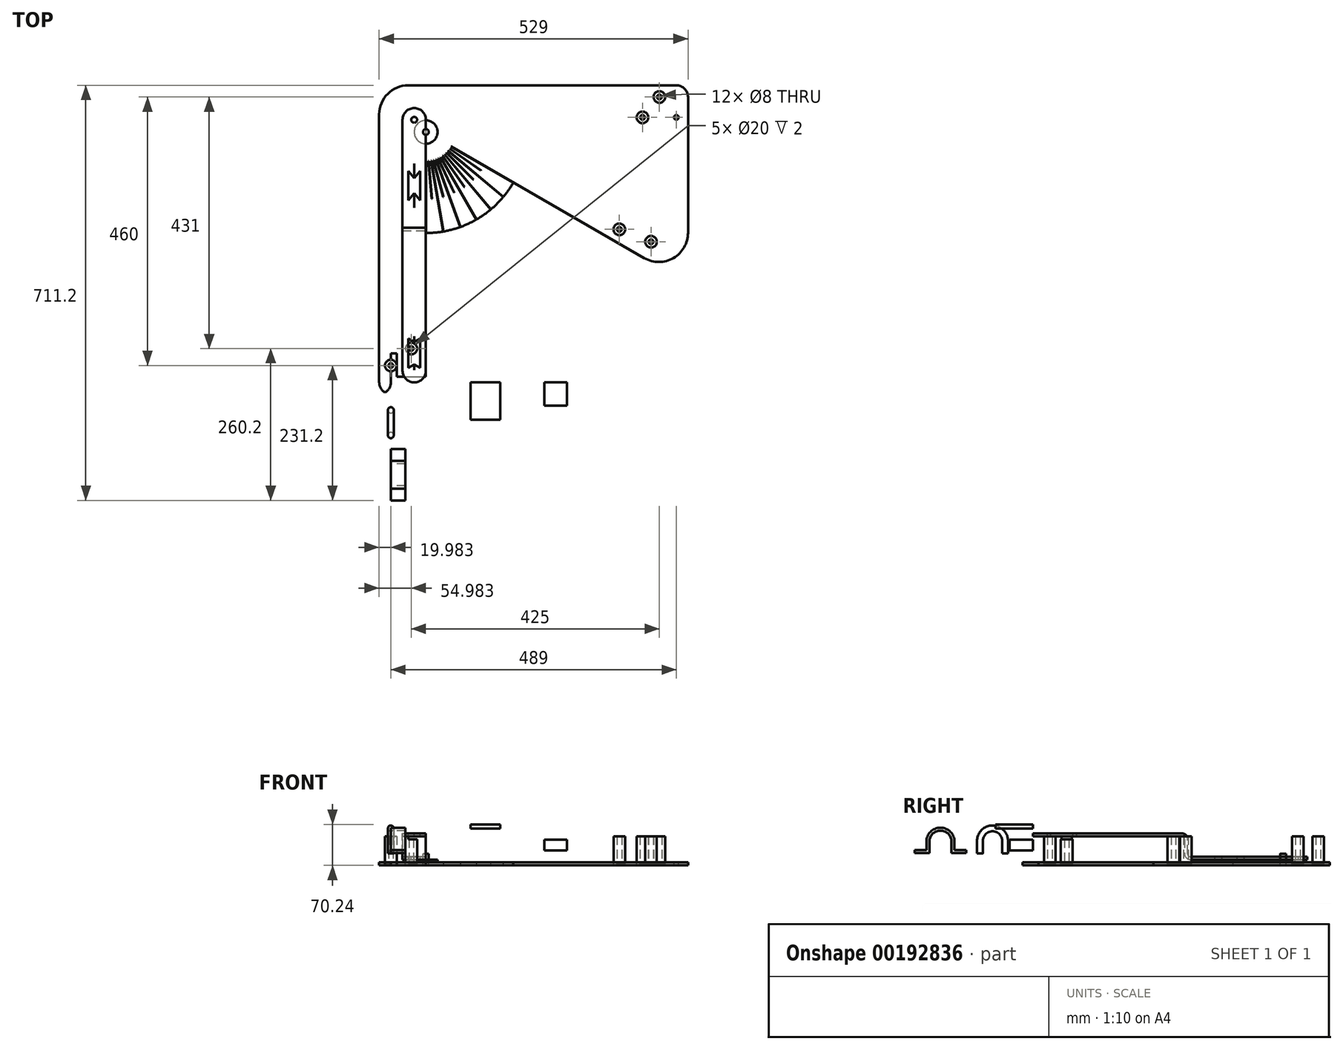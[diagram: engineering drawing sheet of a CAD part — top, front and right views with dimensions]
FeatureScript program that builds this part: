
annotation { "Feature Type Name" : "Feature", "Feature Type Description" : "" }
export const myFeature = defineFeature(function(context is Context, id is Id, definition is map)
    precondition{}
    {
        {
            var Q0;
            Q0=qCreatedBy(makeId("Top.planeOp"),FACE);
            var sketch = newSketch(context, id + "F0", { "sketchPlane" : qUnion([Q0])});
            skLineSegment(sketch, "E0.bottom", {"start": v(0, 0) * mm, "end": v(489, 0) * mm});
            skLineSegment(sketch, "E0.left", {"start": v(0, 0) * mm, "end": v(0, 500) * mm});
            skLineSegment(sketch, "E0.right", {"start": v(489, 0) * mm, "end": v(489, 479) * mm});
            skLineSegment(sketch, "E1.top", {"start": v(0, 0) * mm, "end": v(10, 0) * mm});
            skLineSegment(sketch, "E1.left", {"start": v(0, 489) * mm, "end": v(0, 0) * mm});
            skLineSegment(sketch, "E1.right", {"start": v(10, 50) * mm, "end": v(10, 10) * mm});
            skPoint(sketch, "E2", {"position": v(60, 429) * mm});
            skLineSegment(sketch, "E3", {"start": v(60, 255.9) * mm, "end": v(60, 0) * mm});
            skLineSegment(sketch, "E4", {"start": v(209.9, 342.45) * mm, "end": v(489, 181.32) * mm});
            skLineSegment(sketch, "E5.bottom", {"start": v(10, 48) * mm, "end": v(60, 48) * mm, "construction": true});
            skLineSegment(sketch, "E5.right", {"start": v(60, 48) * mm, "end": v(60, 10) * mm, "construction": true});
            skLineSegment(sketch, "E6.top", {"start": v(441, 429) * mm, "end": v(479, 429) * mm, "construction": true});
            skLineSegment(sketch, "E6.left", {"start": v(441, 479) * mm, "end": v(441, 429) * mm, "construction": true});
            skArc(sketch, "E7", {"start": v(60, 29) * mm, "mid": v(342.84, 146.16) * mm, "end": v(460, 429) * mm, "construction": true});
            skPoint(sketch, "E8", {"position": v(10, 29) * mm});
            skPoint(sketch, "E9", {"position": v(460, 479) * mm});
            skArc(sketch, "E10.0", {"start": v(60, 10) * mm, "mid": v(356.28, 132.72) * mm, "end": v(479, 429) * mm, "construction": true});
            skArc(sketch, "E11.0", {"start": v(60, 48) * mm, "mid": v(329.4, 159.6) * mm, "end": v(441, 429) * mm, "construction": true});
            skLineSegment(sketch, "E12", {"start": v(60, 255.9) * mm, "end": v(209.9, 342.45) * mm, "construction": true});
            skPoint(sketch, "E13.end.orphan", {"position": v(189.9, 354) * mm});
            skPoint(sketch, "E13.start.orphan", {"position": v(60, 279) * mm});
            skCircle(sketch, "E14", {"center": v(60, 429) * mm, "radius": 5 * mm});
            skLineSegment(sketch, "E15.top", {"start": v(489, 489) * mm, "end": v(0, 489) * mm});
            skLineSegment(sketch, "E15.left", {"start": v(489, 479) * mm, "end": v(489, 489) * mm});
            skLineSegment(sketch, "E16", {"start": v(439, 489) * mm, "end": v(439, 479) * mm});
            skLineSegment(sketch, "E17", {"start": v(439, 479) * mm, "end": v(479, 479) * mm});
            skLineSegment(sketch, "E18", {"start": v(479, 479) * mm, "end": v(479, 429) * mm});
            skLineSegment(sketch, "E19", {"start": v(489, 429) * mm, "end": v(479, 429) * mm});
            skArc(sketch, "E20", {"start": v(60, 255.9) * mm, "mid": v(146.55, 279.1) * mm, "end": v(209.9, 342.45) * mm});
            skLineSegment(sketch, "E21", {"start": v(0, 50) * mm, "end": v(10, 50) * mm});
            skLineSegment(sketch, "E22", {"start": v(10, 10) * mm, "end": v(60, 10) * mm});
            skLineSegment(sketch, "E23", {"start": v(60, 0) * mm, "end": v(60, -20) * mm});
            skLineSegment(sketch, "E24", {"start": v(60, -20) * mm, "end": v(0, -20) * mm});
            skLineSegment(sketch, "E25", {"start": v(0, -20) * mm, "end": v(0, 0) * mm});
            skLineSegment(sketch, "E26", {"start": v(0, 489) * mm, "end": v(-20, 489) * mm});
            skLineSegment(sketch, "E27", {"start": v(-20, 489) * mm, "end": v(-20, -20) * mm});
            skLineSegment(sketch, "E28", {"start": v(-20, -20) * mm, "end": v(0, -20) * mm});
            skLineSegment(sketch, "E29", {"start": v(489, 181.32) * mm, "end": v(509, 169.77) * mm});
            skLineSegment(sketch, "E30", {"start": v(509, 169.77) * mm, "end": v(509, 489) * mm});
            skLineSegment(sketch, "E31", {"start": v(509, 489) * mm, "end": v(489, 489) * mm});
            skLineSegment(sketch, "E32", {"start": v(509, 489) * mm, "end": v(509, 509) * mm});
            skLineSegment(sketch, "E33", {"start": v(509, 509) * mm, "end": v(-20, 509) * mm});
            skLineSegment(sketch, "E34", {"start": v(-20, 509) * mm, "end": v(-20, 489) * mm});
            skSolve(sketch);
        }
        {
            var Q0;
            {var subQ3=sQuery(id+"F0.wireOp",EDGE,"E1.right");Q0=makeQuery(id+"F0.imprint","IMPRINT",FACE,{"disambiguationData":[TD([[makeQuery(id+"F0.imprint","IMPRINT",EDGE,{"derivedFrom":subQ3}),1.0]])]});}
            var Q1;
            {var subQ2=sQuery(id+"F0.wireOp",EDGE,"E1.top");Q1=makeQuery(id+"F0.imprint","IMPRINT",FACE,{"disambiguationData":[TD([[makeQuery(id+"F0.imprint","IMPRINT",EDGE,{"derivedFrom":subQ2}),1.0]])]});}
            var Q2;
            {var subQ1=sQuery(id+"F0.wireOp",EDGE,"E15.left");Q2=makeQuery(id+"F0.imprint","IMPRINT",FACE,{"disambiguationData":[TD([[makeQuery(id+"F0.imprint","IMPRINT",EDGE,{"derivedFrom":subQ1}),1.0]])]});}
            var Q3;
            {var subQ1=sQuery(id+"F0.wireOp",EDGE,"E25");Q3=makeQuery(id+"F0.imprint","IMPRINT",FACE,{"disambiguationData":[TD([[makeQuery(id+"F0.imprint","IMPRINT",EDGE,{"derivedFrom":subQ1}),1.0]])]});}
            var Q4;
            {var subQ0=sQuery(id+"F0.wireOp",EDGE,"E1.top");Q4=makeQuery(id+"F0.imprint","IMPRINT",FACE,{"disambiguationData":[TD([[makeQuery(id+"F0.imprint","IMPRINT",EDGE,{"derivedFrom":subQ0}),-1.0]])]});}
            var Q5;
            {var subQ3=sQuery(id+"F0.wireOp",EDGE,"E26");Q5=makeQuery(id+"F0.imprint","IMPRINT",FACE,{"disambiguationData":[TD([[makeQuery(id+"F0.imprint","IMPRINT",EDGE,{"derivedFrom":subQ3}),-1.0]])]});}
            var Q6;
            {var subQ1=sQuery(id+"F0.wireOp",EDGE,"E15.left");Q6=makeQuery(id+"F0.imprint","IMPRINT",FACE,{"disambiguationData":[TD([[makeQuery(id+"F0.imprint","IMPRINT",EDGE,{"derivedFrom":subQ1}),-1.0]])]});}
            extrude(context, id + "F1", {"entities" : qUnion([Q0, Q1, Q2, Q3, Q4, Q5, Q6]), "depth" : 5 * mm});
        }
        {
            var Q0;
            Q0=makeQuery(id+"F1.opExtrude","SWEPT_FACE",FACE,{"disambiguationData":[OSD([sQuery(id+"F0.wireOp",EDGE,"E33")])]});
            cPlane(context, id + "F2", {"entities" : qUnion([Q0]), "cplaneType" : CPlaneType.OFFSET, "offset" : 80 * mm, "oppositeDirection" : true, "width" : 150 * mm, "height" : 150 * mm});
        }
        {
            var Q0;
            Q0=qCreatedBy(id+"F2.planeOp",FACE);
            var sketch = newSketch(context, id + "F3", { "sketchPlane" : qUnion([Q0])});
            skLineSegment(sketch, "E35", {"start": v(-60, 20) * mm, "end": v(-60, 0) * mm});
            skLineSegment(sketch, "E36", {"start": v(-60, 20) * mm, "end": v(-65, 20) * mm});
            skLineSegment(sketch, "E37", {"start": v(-65, 20) * mm, "end": v(-65, 10) * mm});
            skLineSegment(sketch, "E38", {"start": v(-65, 10) * mm, "end": v(-80, 10) * mm});
            skLineSegment(sketch, "E39", {"start": v(-80, 10) * mm, "end": v(-80, 5) * mm});
            skLineSegment(sketch, "E40", {"start": v(-80, 5) * mm, "end": v(-65, 5) * mm});
            skLineSegment(sketch, "E41", {"start": v(-65, 5) * mm, "end": v(-65, 0) * mm});
            skLineSegment(sketch, "E42", {"start": v(-65, 0) * mm, "end": v(-60, 0) * mm});
            skSolve(sketch);
        }
        {
            var Q0;
            Q0=qSketchRegion(id+"F3",true);
            var Q1;
            Q1=sQuery(id+"F3.wireOp",EDGE,"E35");
            revolve(context, id + "F4", {"entities" : qUnion([Q0]), "axis" : qUnion([Q1]), "revolveType" : RevolveType.FULL});
        }
        {
            var Q0;
            Q0=makeQuery(id+"F1.opExtrude","CAP_FACE",FACE,{"disambiguationData":[OSD([sQuery(id+"F0.wireOp",EDGE,"E0.bottom"),sQuery(id+"F0.wireOp",EDGE,"E0.top"),sQuery(id+"F0.wireOp",EDGE,"E0.right"),sQuery(id+"F0.wireOp",EDGE,"E1.right"),sQuery(id+"F0.wireOp",EDGE,"E3"),sQuery(id+"F0.wireOp",EDGE,"E4"),sQuery(id+"F0.wireOp",EDGE,"E12"),sQuery(id+"F0.wireOp",EDGE,"E14")])],"isStart":false});
            cPlane(context, id + "F5", {"entities" : qUnion([Q0]), "cplaneType" : CPlaneType.OFFSET, "offset" : 0 * mm, "width" : 150 * mm, "height" : 150 * mm});
        }
        {
            var Q0;
            Q0=qCreatedBy(id+"F5.planeOp",FACE);
            var sketch = newSketch(context, id + "F6", { "sketchPlane" : qUnion([Q0])});
            skCircle(sketch, "E43", {"center": v(34.98, 58) * mm, "radius": 10 * mm});
            skLineSegment(sketch, "E44.bottom", {"start": v(9.98, 10) * mm, "end": v(59.98, 10) * mm, "construction": true});
            skLineSegment(sketch, "E44.top", {"start": v(9.98, 48) * mm, "end": v(59.98, 48) * mm, "construction": true});
            skLineSegment(sketch, "E44.left", {"start": v(9.98, 10) * mm, "end": v(9.98, 48) * mm, "construction": true});
            skLineSegment(sketch, "E44.right", {"start": v(59.98, 10) * mm, "end": v(59.98, 48) * mm, "construction": true});
            skLineSegment(sketch, "E45.bottom", {"start": v(478.98, 479) * mm, "end": v(440.98, 479) * mm, "construction": true});
            skLineSegment(sketch, "E45.top", {"start": v(478.98, 429) * mm, "end": v(440.98, 429) * mm, "construction": true});
            skLineSegment(sketch, "E45.left", {"start": v(478.98, 479) * mm, "end": v(478.98, 429) * mm, "construction": true});
            skLineSegment(sketch, "E45.right", {"start": v(440.98, 479) * mm, "end": v(440.98, 429) * mm, "construction": true});
            skArc(sketch, "E46", {"start": v(59.98, 29) * mm, "mid": v(342.83, 146.16) * mm, "end": v(459.98, 429) * mm, "construction": true});
            skArc(sketch, "E47.0", {"start": v(59.98, 10) * mm, "mid": v(356.26, 132.72) * mm, "end": v(478.98, 429) * mm, "construction": true});
            skArc(sketch, "E48.0", {"start": v(59.98, 48) * mm, "mid": v(329.4, 159.6) * mm, "end": v(440.98, 429) * mm, "construction": true});
            skLineSegment(sketch, "E49", {"start": v(459.98, 429) * mm, "end": v(459.98, 479) * mm, "construction": true});
            skLineSegment(sketch, "E50", {"start": v(59.98, 29) * mm, "end": v(9.98, 29) * mm, "construction": true});
            skCircle(sketch, "E51", {"center": v(430.98, 454) * mm, "radius": 10 * mm});
            skCircle(sketch, "E52", {"center": v(445.6, 241.01) * mm, "radius": 10 * mm});
            skLineSegment(sketch, "E53", {"start": v(445.6, 241.01) * mm, "end": v(391.37, 262.2) * mm, "construction": true});
            skCircle(sketch, "E54", {"center": v(391.37, 262.2) * mm, "radius": 10 * mm});
            skCircle(sketch, "E55.MirrorC", {"center": v(34.98, 0) * mm, "radius": 10 * mm});
            skCircle(sketch, "E56", {"center": v(-0.02, 29) * mm, "radius": 10 * mm});
            skLineSegment(sketch, "E57", {"start": v(34.98, 0) * mm, "end": v(34.98, 48) * mm, "construction": true});
            skCircle(sketch, "E58.MirrorC", {"center": v(488.98, 454) * mm, "radius": 10 * mm});
            skLineSegment(sketch, "E59", {"start": v(430.98, 454) * mm, "end": v(488.98, 454) * mm, "construction": true});
            skCircle(sketch, "E60", {"center": v(459.98, 489) * mm, "radius": 10 * mm});
            skCircle(sketch, "E61", {"center": v(459.98, 489) * mm, "radius": 4 * mm});
            skCircle(sketch, "E62", {"center": v(488.98, 454) * mm, "radius": 4 * mm});
            skCircle(sketch, "E63", {"center": v(430.98, 454) * mm, "radius": 4 * mm});
            skCircle(sketch, "E64", {"center": v(445.6, 241.01) * mm, "radius": 4 * mm});
            skCircle(sketch, "E65", {"center": v(391.37, 262.2) * mm, "radius": 4 * mm});
            skCircle(sketch, "E66", {"center": v(34.98, 58) * mm, "radius": 4 * mm});
            skCircle(sketch, "E67", {"center": v(34.98, 0) * mm, "radius": 4 * mm});
            skCircle(sketch, "E68", {"center": v(-0.02, 29) * mm, "radius": 4 * mm});
            skSolve(sketch);
        }
        {
            var Q0;
            Q0=makeQuery(id+"F6.imprint","IMPRINT",FACE,{"disambiguationData":[TD([[makeQuery(id+"F6.imprint","IMPRINT",EDGE,{"derivedFrom":sQuery(id+"F6.wireOp",EDGE,"E58.MirrorC")}),-1.0]])]});
            var Q1;
            Q1=makeQuery(id+"F6.imprint","IMPRINT",FACE,{"disambiguationData":[TD([[makeQuery(id+"F6.imprint","IMPRINT",EDGE,{"derivedFrom":sQuery(id+"F6.wireOp",EDGE,"E60")}),1.0]])]});
            var Q2;
            Q2=makeQuery(id+"F6.imprint","IMPRINT",FACE,{"disambiguationData":[TD([[makeQuery(id+"F6.imprint","IMPRINT",EDGE,{"derivedFrom":sQuery(id+"F6.wireOp",EDGE,"E51")}),1.0]])]});
            var Q3;
            Q3=makeQuery(id+"F6.imprint","IMPRINT",FACE,{"disambiguationData":[TD([[makeQuery(id+"F6.imprint","IMPRINT",EDGE,{"derivedFrom":sQuery(id+"F6.wireOp",EDGE,"E52")}),1.0]])]});
            var Q4;
            Q4=makeQuery(id+"F6.imprint","IMPRINT",FACE,{"disambiguationData":[TD([[makeQuery(id+"F6.imprint","IMPRINT",EDGE,{"derivedFrom":sQuery(id+"F6.wireOp",EDGE,"E54")}),1.0]])]});
            var Q5;
            Q5=makeQuery(id+"F6.imprint","IMPRINT",FACE,{"disambiguationData":[TD([[makeQuery(id+"F6.imprint","IMPRINT",EDGE,{"derivedFrom":sQuery(id+"F6.wireOp",EDGE,"E55.MirrorC")}),-1.0]])]});
            var Q6;
            Q6=makeQuery(id+"F6.imprint","IMPRINT",FACE,{"disambiguationData":[TD([[makeQuery(id+"F6.imprint","IMPRINT",EDGE,{"derivedFrom":sQuery(id+"F6.wireOp",EDGE,"E43")}),1.0]])]});
            var Q7;
            Q7=makeQuery(id+"F6.imprint","IMPRINT",FACE,{"disambiguationData":[TD([[makeQuery(id+"F6.imprint","IMPRINT",EDGE,{"derivedFrom":sQuery(id+"F6.wireOp",EDGE,"E56")}),1.0]])]});
            extrude(context, id + "F7", {"entities" : qUnion([Q0, Q1, Q2, Q3, Q4, Q5, Q6, Q7]), "operationType" : NewBodyOperationType.REMOVE, "oppositeDirection" : true, "depth" : 2 * mm});
        }
        {
            var Q0;
            Q0=makeQuery(id+"F6.imprint","IMPRINT",FACE,{"disambiguationData":[TD([[makeQuery(id+"F6.imprint","IMPRINT",EDGE,{"derivedFrom":sQuery(id+"F6.wireOp",EDGE,"E58.MirrorC")}),-1.0]])]});
            var Q1;
            Q1=makeQuery(id+"F6.imprint","IMPRINT",FACE,{"disambiguationData":[TD([[makeQuery(id+"F6.imprint","IMPRINT",EDGE,{"derivedFrom":sQuery(id+"F6.wireOp",EDGE,"E60")}),1.0]])]});
            var Q2;
            Q2=makeQuery(id+"F6.imprint","IMPRINT",FACE,{"disambiguationData":[TD([[makeQuery(id+"F6.imprint","IMPRINT",EDGE,{"derivedFrom":sQuery(id+"F6.wireOp",EDGE,"E51")}),1.0]])]});
            var Q3;
            Q3=makeQuery(id+"F6.imprint","IMPRINT",FACE,{"disambiguationData":[TD([[makeQuery(id+"F6.imprint","IMPRINT",EDGE,{"derivedFrom":sQuery(id+"F6.wireOp",EDGE,"E52")}),1.0]])]});
            var Q4;
            Q4=makeQuery(id+"F6.imprint","IMPRINT",FACE,{"disambiguationData":[TD([[makeQuery(id+"F6.imprint","IMPRINT",EDGE,{"derivedFrom":sQuery(id+"F6.wireOp",EDGE,"E54")}),1.0]])]});
            var Q5;
            Q5=makeQuery(id+"F6.imprint","IMPRINT",FACE,{"disambiguationData":[TD([[makeQuery(id+"F6.imprint","IMPRINT",EDGE,{"derivedFrom":sQuery(id+"F6.wireOp",EDGE,"E56")}),1.0]])]});
            var Q6;
            Q6=makeQuery(id+"F6.imprint","IMPRINT",FACE,{"disambiguationData":[TD([[makeQuery(id+"F6.imprint","IMPRINT",EDGE,{"derivedFrom":sQuery(id+"F6.wireOp",EDGE,"E55.MirrorC")}),-1.0]])]});
            var Q7;
            Q7=makeQuery(id+"F6.imprint","IMPRINT",FACE,{"disambiguationData":[TD([[makeQuery(id+"F6.imprint","IMPRINT",EDGE,{"derivedFrom":sQuery(id+"F6.wireOp",EDGE,"E43")}),1.0]])]});
            extrude(context, id + "F8", {"entities" : qUnion([Q0, Q1, Q2, Q3, Q4, Q5, Q6, Q7]), "depth" : 44.85 * mm});
        }
        {
            var Q0;
            Q0=makeQuery(id+"F1.opExtrude","CAP_FACE",FACE,{"disambiguationData":[OSD([sQuery(id+"F0.wireOp",EDGE,"E0.bottom"),sQuery(id+"F0.wireOp",EDGE,"E0.right"),sQuery(id+"F0.wireOp",EDGE,"E1.right"),sQuery(id+"F0.wireOp",EDGE,"E3"),sQuery(id+"F0.wireOp",EDGE,"E4"),sQuery(id+"F0.wireOp",EDGE,"E12"),sQuery(id+"F0.wireOp",EDGE,"E14"),sQuery(id+"F0.wireOp",EDGE,"E15.top"),sQuery(id+"F0.wireOp",EDGE,"E16"),sQuery(id+"F0.wireOp",EDGE,"E17"),sQuery(id+"F0.wireOp",EDGE,"E18"),sQuery(id+"F0.wireOp",EDGE,"E19")])],"isStart":false});
            var sketch = newSketch(context, id + "F9", { "sketchPlane" : qUnion([Q0])});
            skLineSegment(sketch, "E69", {"start": v(60, 379) * mm, "end": v(60, 255.9) * mm});
            skLineSegment(sketch, "E70", {"start": v(103.3, 404) * mm, "end": v(209.9, 342.45) * mm});
            skArc(sketch, "E71", {"start": v(60, 314) * mm, "mid": v(117.5, 329.4) * mm, "end": v(159.6, 371.5) * mm});
            skLineSegment(sketch, "E72.0", {"start": v(64.45, 426.72) * mm, "end": v(210.03, 342.67) * mm});
            skArc(sketch, "E73", {"start": v(60, 424) * mm, "mid": v(62.6, 424.73) * mm, "end": v(64.45, 426.72) * mm});
            skLineSegment(sketch, "E74.trimOffspring", {"start": v(64.2, 426.29) * mm, "end": v(64.83, 425.92) * mm});
            skLineSegment(sketch, "E75", {"start": v(210.03, 342.67) * mm, "end": v(209.9, 342.45) * mm});
            skLineSegment(sketch, "E76", {"start": v(100.96, 400.32) * mm, "end": v(154.2, 363.04) * mm});
            skLineSegment(sketch, "E77", {"start": v(98.3, 396.86) * mm, "end": v(192.6, 317.74) * mm});
            skLineSegment(sketch, "E78", {"start": v(95.36, 393.64) * mm, "end": v(141.32, 347.68) * mm});
            skLineSegment(sketch, "E79", {"start": v(92.14, 390.7) * mm, "end": v(171.26, 296.4) * mm});
            skLineSegment(sketch, "E80", {"start": v(88.68, 388.04) * mm, "end": v(125.96, 334.8) * mm});
            skLineSegment(sketch, "E81", {"start": v(85, 385.7) * mm, "end": v(146.55, 279.1) * mm});
            skLineSegment(sketch, "E82", {"start": v(81.13, 383.68) * mm, "end": v(108.6, 324.77) * mm});
            skLineSegment(sketch, "E83", {"start": v(77.1, 382.02) * mm, "end": v(119.2, 266.34) * mm});
            skLineSegment(sketch, "E84", {"start": v(72.94, 380.7) * mm, "end": v(89.76, 317.92) * mm});
            skLineSegment(sketch, "E85", {"start": v(68.68, 379.76) * mm, "end": v(90.06, 258.54) * mm});
            skLineSegment(sketch, "E86", {"start": v(64.36, 379.2) * mm, "end": v(70.02, 314.44) * mm});
            skArc(sketch, "E87", {"start": v(60, 255.9) * mm, "mid": v(146.55, 279.1) * mm, "end": v(209.9, 342.45) * mm, "construction": true});
            skPoint(sketch, "E88.orphan", {"position": v(117.5, 329.4) * mm});
            skLineSegment(sketch, "E89.0", {"start": v(64.24, 426.34) * mm, "end": v(64.83, 425.92) * mm});
            skLineSegment(sketch, "E90.0", {"start": v(63.95, 425.93) * mm, "end": v(64.55, 425.51) * mm});
            skLineSegment(sketch, "E91.0", {"start": v(63.67, 425.6) * mm, "end": v(64.23, 425.13) * mm});
            skLineSegment(sketch, "E92.0", {"start": v(64, 425.98) * mm, "end": v(64.55, 425.51) * mm});
            skLineSegment(sketch, "E93.0", {"start": v(63.36, 425.29) * mm, "end": v(63.87, 424.77) * mm});
            skLineSegment(sketch, "E94.0", {"start": v(63.71, 425.64) * mm, "end": v(64.23, 425.13) * mm});
            skLineSegment(sketch, "E95.0", {"start": v(63.02, 425) * mm, "end": v(63.49, 424.45) * mm});
            skLineSegment(sketch, "E96.0", {"start": v(63.4, 425.33) * mm, "end": v(63.87, 424.77) * mm});
            skLineSegment(sketch, "E97.0", {"start": v(63.07, 425.05) * mm, "end": v(63.49, 424.45) * mm});
            skLineSegment(sketch, "E98.0", {"start": v(62.66, 424.76) * mm, "end": v(63.08, 424.17) * mm});
            skLineSegment(sketch, "E99.0", {"start": v(55.7, 435.96) * mm, "end": v(62.65, 423.92) * mm});
            skLineSegment(sketch, "E100.0", {"start": v(56.12, 436.21) * mm, "end": v(63.08, 424.17) * mm});
            skLineSegment(sketch, "E101.0", {"start": v(61.89, 424.36) * mm, "end": v(62.2, 423.7) * mm});
            skLineSegment(sketch, "E102.0", {"start": v(62.34, 424.57) * mm, "end": v(62.65, 423.92) * mm});
            skLineSegment(sketch, "E103.0", {"start": v(61.48, 424.22) * mm, "end": v(61.72, 423.53) * mm});
            skLineSegment(sketch, "E104.0", {"start": v(61.95, 424.39) * mm, "end": v(62.2, 423.7) * mm});
            skLineSegment(sketch, "E105.0", {"start": v(61.05, 424.1) * mm, "end": v(61.24, 423.4) * mm});
            skLineSegment(sketch, "E106.0", {"start": v(61.54, 424.24) * mm, "end": v(61.72, 423.53) * mm});
            skLineSegment(sketch, "E107.0", {"start": v(60.62, 424.03) * mm, "end": v(60.75, 423.32) * mm});
            skLineSegment(sketch, "E108.0", {"start": v(61.11, 424.12) * mm, "end": v(61.24, 423.4) * mm});
            skLineSegment(sketch, "E109.0", {"start": v(60.19, 424) * mm, "end": v(60.25, 423.27) * mm});
            skLineSegment(sketch, "E110.0", {"start": v(60.68, 424.04) * mm, "end": v(60.75, 423.32) * mm});
            skLineSegment(sketch, "E111.0", {"start": v(59.75, 429) * mm, "end": v(59.75, 255.9) * mm});
            skLineSegment(sketch, "E112.0", {"start": v(60.25, 424) * mm, "end": v(60.25, 423.27) * mm});
            skArc(sketch, "E113", {"start": v(103.3, 404) * mm, "mid": v(85, 385.7) * mm, "end": v(60, 379) * mm});
            skLineSegment(sketch, "E114.trimOffspring", {"start": v(60.25, 379) * mm, "end": v(60.25, 255.9) * mm});
            skLineSegment(sketch, "E115.trimOffspring", {"start": v(64.1, 379.17) * mm, "end": v(69.77, 314.42) * mm});
            skLineSegment(sketch, "E116.trimOffspring", {"start": v(64.6, 379.21) * mm, "end": v(70.27, 314.46) * mm});
            skLineSegment(sketch, "E117.trimOffspring", {"start": v(68.44, 379.72) * mm, "end": v(89.81, 258.5) * mm});
            skLineSegment(sketch, "E118.trimOffspring", {"start": v(68.93, 379.8) * mm, "end": v(90.3, 258.58) * mm});
            skLineSegment(sketch, "E119.trimOffspring", {"start": v(72.7, 380.64) * mm, "end": v(89.52, 317.85) * mm});
            skLineSegment(sketch, "E120.trimOffspring", {"start": v(73.18, 380.77) * mm, "end": v(90, 317.98) * mm});
            skLineSegment(sketch, "E121.trimOffspring", {"start": v(76.87, 381.93) * mm, "end": v(118.97, 266.26) * mm});
            skLineSegment(sketch, "E122.trimOffspring", {"start": v(77.34, 382.1) * mm, "end": v(119.44, 266.43) * mm});
            skLineSegment(sketch, "E123.trimOffspring", {"start": v(80.9, 383.58) * mm, "end": v(108.37, 324.67) * mm});
            skLineSegment(sketch, "E124.trimOffspring", {"start": v(81.36, 383.8) * mm, "end": v(108.83, 324.88) * mm});
            skLineSegment(sketch, "E125.trimOffspring", {"start": v(88.47, 387.9) * mm, "end": v(125.76, 334.65) * mm});
            skLineSegment(sketch, "E126.trimOffspring", {"start": v(88.88, 388.19) * mm, "end": v(126.17, 334.94) * mm});
            skLineSegment(sketch, "E127.trimOffspring", {"start": v(84.78, 385.57) * mm, "end": v(146.33, 278.97) * mm});
            skLineSegment(sketch, "E128.trimOffspring", {"start": v(85.22, 385.82) * mm, "end": v(146.76, 279.22) * mm});
            skLineSegment(sketch, "E129.trimOffspring", {"start": v(91.95, 390.54) * mm, "end": v(171.07, 296.24) * mm});
            skLineSegment(sketch, "E130.trimOffspring", {"start": v(92.33, 390.86) * mm, "end": v(171.45, 296.56) * mm});
            skLineSegment(sketch, "E131.trimOffspring", {"start": v(95.18, 393.47) * mm, "end": v(141.14, 347.5) * mm});
            skLineSegment(sketch, "E132.trimOffspring", {"start": v(95.53, 393.82) * mm, "end": v(141.5, 347.86) * mm});
            skLineSegment(sketch, "E133.trimOffspring", {"start": v(98.14, 396.67) * mm, "end": v(192.44, 317.55) * mm});
            skLineSegment(sketch, "E134.trimOffspring", {"start": v(98.46, 397.05) * mm, "end": v(192.76, 317.93) * mm});
            skLineSegment(sketch, "E135.trimOffspring", {"start": v(100.81, 400.12) * mm, "end": v(154.06, 362.83) * mm});
            skLineSegment(sketch, "E136.trimOffspring", {"start": v(101.1, 400.53) * mm, "end": v(154.35, 363.24) * mm});
            skLineSegment(sketch, "E137.trimOffspring", {"start": v(103.18, 403.78) * mm, "end": v(209.78, 342.24) * mm});
            skArc(sketch, "E138", {"start": v(209.9, 342.45) * mm, "mid": v(146.55, 279.1) * mm, "end": v(60, 255.9) * mm});
            skSolve(sketch);
        }
        {
            var Q0;
            {var subQ0=sQuery(id+"F9.wireOp",EDGE,"E113");var subQ1=sQuery(id+"F9.wireOp",EDGE,"E70");var subQ2=makeQuery(id+"F9.imprint","INTERSECT",VERTEX,{"derivedFrom":[subQ1,subQ0]});Q0=makeQuery(id+"F9.imprint","IMPRINT",FACE,{"disambiguationData":[TD([[makeQuery(id+"F9.imprint","IMPRINT",EDGE,{"disambiguationData":[TD([[subQ2,-1.0]])],"derivedFrom":subQ1}),-1.0]])]});}
            var Q1;
            {var subQ0=sQuery(id+"F9.wireOp",EDGE,"E70");var subQ3=sQuery(id+"F9.wireOp",EDGE,"E71");var subQ4=makeQuery(id+"F9.imprint","INTERSECT",VERTEX,{"derivedFrom":[subQ0,subQ3]});Q1=makeQuery(id+"F9.imprint","IMPRINT",FACE,{"disambiguationData":[TD([[makeQuery(id+"F9.imprint","IMPRINT",EDGE,{"disambiguationData":[TD([[subQ4,1.0]])],"derivedFrom":subQ3}),-1.0]])]});}
            var Q2;
            {var subQ0=sQuery(id+"F9.wireOp",EDGE,"E76");Q2=makeQuery(id+"F9.imprint","IMPRINT",FACE,{"disambiguationData":[TD([[makeQuery(id+"F9.imprint","IMPRINT",EDGE,{"derivedFrom":subQ0}),1.0]])]});}
            var Q3;
            {var subQ0=sQuery(id+"F9.wireOp",EDGE,"E76");Q3=makeQuery(id+"F9.imprint","IMPRINT",FACE,{"disambiguationData":[TD([[makeQuery(id+"F9.imprint","IMPRINT",EDGE,{"derivedFrom":subQ0}),-1.0]])]});}
            var Q4;
            {var subQ0=sQuery(id+"F9.wireOp",EDGE,"E77");var subQ1=sQuery(id+"F9.wireOp",EDGE,"E71");var subQ2=makeQuery(id+"F9.imprint","INTERSECT",VERTEX,{"derivedFrom":[subQ1,subQ0]});Q4=makeQuery(id+"F9.imprint","IMPRINT",FACE,{"disambiguationData":[TD([[makeQuery(id+"F9.imprint","IMPRINT",EDGE,{"disambiguationData":[TD([[subQ2,-1.0]])],"derivedFrom":subQ1}),1.0]])]});}
            var Q5;
            {var subQ0=sQuery(id+"F9.wireOp",EDGE,"E133.trimOffspring");var subQ1=sQuery(id+"F9.wireOp",EDGE,"E71");var subQ2=makeQuery(id+"F9.imprint","INTERSECT",VERTEX,{"derivedFrom":[subQ1,subQ0]});Q5=makeQuery(id+"F9.imprint","IMPRINT",FACE,{"disambiguationData":[TD([[makeQuery(id+"F9.imprint","IMPRINT",EDGE,{"disambiguationData":[TD([[subQ2,-1.0]])],"derivedFrom":subQ1}),1.0]])]});}
            var Q6;
            {var subQ0=sQuery(id+"F9.wireOp",EDGE,"E133.trimOffspring");var subQ1=sQuery(id+"F9.wireOp",EDGE,"E71");var subQ2=makeQuery(id+"F9.imprint","INTERSECT",VERTEX,{"derivedFrom":[subQ1,subQ0]});Q6=makeQuery(id+"F9.imprint","IMPRINT",FACE,{"disambiguationData":[TD([[makeQuery(id+"F9.imprint","IMPRINT",EDGE,{"disambiguationData":[TD([[subQ2,-1.0]])],"derivedFrom":subQ1}),-1.0]])]});}
            var Q7;
            {var subQ0=sQuery(id+"F9.wireOp",EDGE,"E77");var subQ1=sQuery(id+"F9.wireOp",EDGE,"E71");var subQ2=makeQuery(id+"F9.imprint","INTERSECT",VERTEX,{"derivedFrom":[subQ1,subQ0]});Q7=makeQuery(id+"F9.imprint","IMPRINT",FACE,{"disambiguationData":[TD([[makeQuery(id+"F9.imprint","IMPRINT",EDGE,{"disambiguationData":[TD([[subQ2,-1.0]])],"derivedFrom":subQ1}),-1.0]])]});}
            var Q8;
            {var subQ0=sQuery(id+"F9.wireOp",EDGE,"E78");Q8=makeQuery(id+"F9.imprint","IMPRINT",FACE,{"disambiguationData":[TD([[makeQuery(id+"F9.imprint","IMPRINT",EDGE,{"derivedFrom":subQ0}),-1.0]])]});}
            var Q9;
            {var subQ0=sQuery(id+"F9.wireOp",EDGE,"E78");Q9=makeQuery(id+"F9.imprint","IMPRINT",FACE,{"disambiguationData":[TD([[makeQuery(id+"F9.imprint","IMPRINT",EDGE,{"derivedFrom":subQ0}),1.0]])]});}
            var Q10;
            {var subQ0=sQuery(id+"F9.wireOp",EDGE,"E79");var subQ1=sQuery(id+"F9.wireOp",EDGE,"E71");var subQ2=makeQuery(id+"F9.imprint","INTERSECT",VERTEX,{"derivedFrom":[subQ1,subQ0]});Q10=makeQuery(id+"F9.imprint","IMPRINT",FACE,{"disambiguationData":[TD([[makeQuery(id+"F9.imprint","IMPRINT",EDGE,{"disambiguationData":[TD([[subQ2,-1.0]])],"derivedFrom":subQ1}),1.0]])]});}
            var Q11;
            {var subQ0=sQuery(id+"F9.wireOp",EDGE,"E79");var subQ1=sQuery(id+"F9.wireOp",EDGE,"E71");var subQ2=makeQuery(id+"F9.imprint","INTERSECT",VERTEX,{"derivedFrom":[subQ1,subQ0]});Q11=makeQuery(id+"F9.imprint","IMPRINT",FACE,{"disambiguationData":[TD([[makeQuery(id+"F9.imprint","IMPRINT",EDGE,{"disambiguationData":[TD([[subQ2,-1.0]])],"derivedFrom":subQ1}),-1.0]])]});}
            var Q12;
            {var subQ0=sQuery(id+"F9.wireOp",EDGE,"E129.trimOffspring");var subQ1=sQuery(id+"F9.wireOp",EDGE,"E71");var subQ2=makeQuery(id+"F9.imprint","INTERSECT",VERTEX,{"derivedFrom":[subQ1,subQ0]});Q12=makeQuery(id+"F9.imprint","IMPRINT",FACE,{"disambiguationData":[TD([[makeQuery(id+"F9.imprint","IMPRINT",EDGE,{"disambiguationData":[TD([[subQ2,-1.0]])],"derivedFrom":subQ1}),-1.0]])]});}
            var Q13;
            {var subQ0=sQuery(id+"F9.wireOp",EDGE,"E129.trimOffspring");var subQ1=sQuery(id+"F9.wireOp",EDGE,"E71");var subQ2=makeQuery(id+"F9.imprint","INTERSECT",VERTEX,{"derivedFrom":[subQ1,subQ0]});Q13=makeQuery(id+"F9.imprint","IMPRINT",FACE,{"disambiguationData":[TD([[makeQuery(id+"F9.imprint","IMPRINT",EDGE,{"disambiguationData":[TD([[subQ2,-1.0]])],"derivedFrom":subQ1}),1.0]])]});}
            var Q14;
            {var subQ0=sQuery(id+"F9.wireOp",EDGE,"E80");Q14=makeQuery(id+"F9.imprint","IMPRINT",FACE,{"disambiguationData":[TD([[makeQuery(id+"F9.imprint","IMPRINT",EDGE,{"derivedFrom":subQ0}),1.0]])]});}
            var Q15;
            {var subQ0=sQuery(id+"F9.wireOp",EDGE,"E80");Q15=makeQuery(id+"F9.imprint","IMPRINT",FACE,{"disambiguationData":[TD([[makeQuery(id+"F9.imprint","IMPRINT",EDGE,{"derivedFrom":subQ0}),-1.0]])]});}
            var Q16;
            {var subQ0=sQuery(id+"F9.wireOp",EDGE,"E128.trimOffspring");var subQ1=sQuery(id+"F9.wireOp",EDGE,"E71");var subQ2=makeQuery(id+"F9.imprint","INTERSECT",VERTEX,{"derivedFrom":[subQ1,subQ0]});Q16=makeQuery(id+"F9.imprint","IMPRINT",FACE,{"disambiguationData":[TD([[makeQuery(id+"F9.imprint","IMPRINT",EDGE,{"disambiguationData":[TD([[subQ2,1.0]])],"derivedFrom":subQ1}),1.0]])]});}
            var Q17;
            {var subQ0=sQuery(id+"F9.wireOp",EDGE,"E127.trimOffspring");var subQ1=sQuery(id+"F9.wireOp",EDGE,"E71");var subQ2=makeQuery(id+"F9.imprint","INTERSECT",VERTEX,{"derivedFrom":[subQ1,subQ0]});Q17=makeQuery(id+"F9.imprint","IMPRINT",FACE,{"disambiguationData":[TD([[makeQuery(id+"F9.imprint","IMPRINT",EDGE,{"disambiguationData":[TD([[subQ2,-1.0]])],"derivedFrom":subQ1}),1.0]])]});}
            var Q18;
            {var subQ0=sQuery(id+"F9.wireOp",EDGE,"E82");Q18=makeQuery(id+"F9.imprint","IMPRINT",FACE,{"disambiguationData":[TD([[makeQuery(id+"F9.imprint","IMPRINT",EDGE,{"derivedFrom":subQ0}),-1.0]])]});}
            var Q19;
            {var subQ0=sQuery(id+"F9.wireOp",EDGE,"E82");Q19=makeQuery(id+"F9.imprint","IMPRINT",FACE,{"disambiguationData":[TD([[makeQuery(id+"F9.imprint","IMPRINT",EDGE,{"derivedFrom":subQ0}),1.0]])]});}
            var Q20;
            {var subQ0=sQuery(id+"F9.wireOp",EDGE,"E83");var subQ1=sQuery(id+"F9.wireOp",EDGE,"E71");var subQ2=makeQuery(id+"F9.imprint","INTERSECT",VERTEX,{"derivedFrom":[subQ1,subQ0]});Q20=makeQuery(id+"F9.imprint","IMPRINT",FACE,{"disambiguationData":[TD([[makeQuery(id+"F9.imprint","IMPRINT",EDGE,{"disambiguationData":[TD([[subQ2,-1.0]])],"derivedFrom":subQ1}),1.0]])]});}
            var Q21;
            {var subQ0=sQuery(id+"F9.wireOp",EDGE,"E121.trimOffspring");var subQ1=sQuery(id+"F9.wireOp",EDGE,"E71");var subQ2=makeQuery(id+"F9.imprint","INTERSECT",VERTEX,{"derivedFrom":[subQ1,subQ0]});Q21=makeQuery(id+"F9.imprint","IMPRINT",FACE,{"disambiguationData":[TD([[makeQuery(id+"F9.imprint","IMPRINT",EDGE,{"disambiguationData":[TD([[subQ2,-1.0]])],"derivedFrom":subQ1}),1.0]])]});}
            var Q22;
            {var subQ0=sQuery(id+"F9.wireOp",EDGE,"E121.trimOffspring");var subQ1=sQuery(id+"F9.wireOp",EDGE,"E71");var subQ2=makeQuery(id+"F9.imprint","INTERSECT",VERTEX,{"derivedFrom":[subQ1,subQ0]});Q22=makeQuery(id+"F9.imprint","IMPRINT",FACE,{"disambiguationData":[TD([[makeQuery(id+"F9.imprint","IMPRINT",EDGE,{"disambiguationData":[TD([[subQ2,-1.0]])],"derivedFrom":subQ1}),-1.0]])]});}
            var Q23;
            {var subQ0=sQuery(id+"F9.wireOp",EDGE,"E83");var subQ1=sQuery(id+"F9.wireOp",EDGE,"E71");var subQ2=makeQuery(id+"F9.imprint","INTERSECT",VERTEX,{"derivedFrom":[subQ1,subQ0]});Q23=makeQuery(id+"F9.imprint","IMPRINT",FACE,{"disambiguationData":[TD([[makeQuery(id+"F9.imprint","IMPRINT",EDGE,{"disambiguationData":[TD([[subQ2,-1.0]])],"derivedFrom":subQ1}),-1.0]])]});}
            var Q24;
            {var subQ0=sQuery(id+"F9.wireOp",EDGE,"E84");Q24=makeQuery(id+"F9.imprint","IMPRINT",FACE,{"disambiguationData":[TD([[makeQuery(id+"F9.imprint","IMPRINT",EDGE,{"derivedFrom":subQ0}),1.0]])]});}
            var Q25;
            {var subQ0=sQuery(id+"F9.wireOp",EDGE,"E84");Q25=makeQuery(id+"F9.imprint","IMPRINT",FACE,{"disambiguationData":[TD([[makeQuery(id+"F9.imprint","IMPRINT",EDGE,{"derivedFrom":subQ0}),-1.0]])]});}
            var Q26;
            {var subQ0=sQuery(id+"F9.wireOp",EDGE,"E85");var subQ1=sQuery(id+"F9.wireOp",EDGE,"E71");var subQ2=makeQuery(id+"F9.imprint","INTERSECT",VERTEX,{"derivedFrom":[subQ1,subQ0]});Q26=makeQuery(id+"F9.imprint","IMPRINT",FACE,{"disambiguationData":[TD([[makeQuery(id+"F9.imprint","IMPRINT",EDGE,{"disambiguationData":[TD([[subQ2,-1.0]])],"derivedFrom":subQ1}),1.0]])]});}
            var Q27;
            {var subQ0=sQuery(id+"F9.wireOp",EDGE,"E117.trimOffspring");var subQ1=sQuery(id+"F9.wireOp",EDGE,"E71");var subQ2=makeQuery(id+"F9.imprint","INTERSECT",VERTEX,{"derivedFrom":[subQ1,subQ0]});Q27=makeQuery(id+"F9.imprint","IMPRINT",FACE,{"disambiguationData":[TD([[makeQuery(id+"F9.imprint","IMPRINT",EDGE,{"disambiguationData":[TD([[subQ2,-1.0]])],"derivedFrom":subQ1}),1.0]])]});}
            var Q28;
            {var subQ0=sQuery(id+"F9.wireOp",EDGE,"E117.trimOffspring");var subQ1=sQuery(id+"F9.wireOp",EDGE,"E71");var subQ2=makeQuery(id+"F9.imprint","INTERSECT",VERTEX,{"derivedFrom":[subQ1,subQ0]});Q28=makeQuery(id+"F9.imprint","IMPRINT",FACE,{"disambiguationData":[TD([[makeQuery(id+"F9.imprint","IMPRINT",EDGE,{"disambiguationData":[TD([[subQ2,-1.0]])],"derivedFrom":subQ1}),-1.0]])]});}
            var Q29;
            {var subQ0=sQuery(id+"F9.wireOp",EDGE,"E85");var subQ1=sQuery(id+"F9.wireOp",EDGE,"E71");var subQ2=makeQuery(id+"F9.imprint","INTERSECT",VERTEX,{"derivedFrom":[subQ1,subQ0]});Q29=makeQuery(id+"F9.imprint","IMPRINT",FACE,{"disambiguationData":[TD([[makeQuery(id+"F9.imprint","IMPRINT",EDGE,{"disambiguationData":[TD([[subQ2,-1.0]])],"derivedFrom":subQ1}),-1.0]])]});}
            var Q30;
            {var subQ0=sQuery(id+"F9.wireOp",EDGE,"E86");Q30=makeQuery(id+"F9.imprint","IMPRINT",FACE,{"disambiguationData":[TD([[makeQuery(id+"F9.imprint","IMPRINT",EDGE,{"derivedFrom":subQ0}),1.0]])]});}
            var Q31;
            {var subQ0=sQuery(id+"F9.wireOp",EDGE,"E86");Q31=makeQuery(id+"F9.imprint","IMPRINT",FACE,{"disambiguationData":[TD([[makeQuery(id+"F9.imprint","IMPRINT",EDGE,{"derivedFrom":subQ0}),-1.0]])]});}
            var Q32;
            {var subQ6=sQuery(id+"F9.wireOp",EDGE,"E69");Q32=makeQuery(id+"F9.imprint","IMPRINT",FACE,{"disambiguationData":[TD([[makeQuery(id+"F9.imprint","IMPRINT",EDGE,{"derivedFrom":subQ6}),1.0]])]});}
            var Q33;
            {var subQ0=sQuery(id+"F9.wireOp",EDGE,"E127.trimOffspring");var subQ1=sQuery(id+"F9.wireOp",EDGE,"E71");var subQ2=makeQuery(id+"F9.imprint","INTERSECT",VERTEX,{"derivedFrom":[subQ1,subQ0]});Q33=makeQuery(id+"F9.imprint","IMPRINT",FACE,{"disambiguationData":[TD([[makeQuery(id+"F9.imprint","IMPRINT",EDGE,{"disambiguationData":[TD([[subQ2,-1.0]])],"derivedFrom":subQ1}),-1.0]])]});}
            var Q34;
            {var subQ0=sQuery(id+"F9.wireOp",EDGE,"E81");var subQ1=sQuery(id+"F9.wireOp",EDGE,"E71");var subQ2=makeQuery(id+"F9.imprint","INTERSECT",VERTEX,{"derivedFrom":[subQ1,subQ0]});Q34=makeQuery(id+"F9.imprint","IMPRINT",FACE,{"disambiguationData":[TD([[makeQuery(id+"F9.imprint","IMPRINT",EDGE,{"disambiguationData":[TD([[subQ2,-1.0]])],"derivedFrom":subQ1}),-1.0]])]});}
            extrude(context, id + "F10", {"entities" : qUnion([Q0, Q1, Q2, Q3, Q4, Q5, Q6, Q7, Q8, Q9, Q10, Q11, Q12, Q13, Q14, Q15, Q16, Q17, Q18, Q19, Q20, Q21, Q22, Q23, Q24, Q25, Q26, Q27, Q28, Q29, Q30, Q31, Q32, Q33, Q34]), "operationType" : NewBodyOperationType.REMOVE, "oppositeDirection" : true, "depth" : 0.5 * mm});
        }
        {
            var Q0;
            Q0=makeQuery(id+"F10.boolean.opBoolean","MERGE",FACE,{"derivedFrom":[makeQuery(id+"F1.opExtrude","SWEPT_FACE",FACE,{"disambiguationData":[OSD([sQuery(id+"F0.wireOp",EDGE,"E3")])]}),makeQuery(id+"F10.opExtrude","SWEPT_FACE",FACE,{"disambiguationData":[OSD([sQuery(id+"F9.wireOp",EDGE,"E69")])]})]});
            var sketch = newSketch(context, id + "F11", { "sketchPlane" : qUnion([Q0])});
            skLineSegment(sketch, "E139.bottom", {"start": v(470, 10) * mm, "end": v(260, 10) * mm});
            skLineSegment(sketch, "E139.top", {"start": v(470, 15) * mm, "end": v(265, 15) * mm});
            skLineSegment(sketch, "E139.left", {"start": v(470, 10) * mm, "end": v(470, 15) * mm});
            skLineSegment(sketch, "E140", {"start": v(265, 15) * mm, "end": v(265, 55) * mm});
            skLineSegment(sketch, "E141", {"start": v(265, 55) * mm, "end": v(0, 55) * mm});
            skLineSegment(sketch, "E142", {"start": v(0, 55) * mm, "end": v(0, 50) * mm});
            skLineSegment(sketch, "E143", {"start": v(0, 50) * mm, "end": v(260, 50) * mm});
            skLineSegment(sketch, "E144", {"start": v(260, 50) * mm, "end": v(260, 10) * mm});
            skPoint(sketch, "E145.trimOffspring.end.orphan", {"position": v(0, 35) * mm});
            skSolve(sketch);
        }
        {
            var Q0;
            Q0=qSketchRegion(id+"F11",true);
            extrude(context, id + "F12", {"entities" : qUnion([Q0]), "oppositeDirection" : true, "depth" : 40 * mm});
        }
        {
            var Q0;
            Q0=makeQuery(id+"F12.opExtrude","SWEPT_FACE",FACE,{"disambiguationData":[OSD([sQuery(id+"F11.wireOp",EDGE,"E139.top")])]});
            var sketch = newSketch(context, id + "F13", { "sketchPlane" : qUnion([Q0])});
            skCircle(sketch, "E146", {"center": v(40, 450) * mm, "radius": 5 * mm});
            skPoint(sketch, "E146.centerSnap0", {"position": v(40, 470) * mm});
            skSolve(sketch);
        }
        {
            var Q0;
            Q0=qSketchRegion(id+"F13",true);
            extrude(context, id + "F14", {"entities" : qUnion([Q0]), "operationType" : NewBodyOperationType.REMOVE, "oppositeDirection" : true, "depth" : 10 * mm});
        }
        {
            var Q0;
            Q0=makeQuery(id+"F12.opExtrude","SWEPT_FACE",FACE,{"disambiguationData":[OSD([sQuery(id+"F11.wireOp",EDGE,"E139.top")])]});
            var sketch = newSketch(context, id + "F15", { "sketchPlane" : qUnion([Q0])});
            skLineSegment(sketch, "E147.bottom", {"start": v(30, 362.1) * mm, "end": v(50, 362.1) * mm});
            skLineSegment(sketch, "E147.top", {"start": v(30, 312.1) * mm, "end": v(50, 312.1) * mm});
            skLineSegment(sketch, "E147.left", {"start": v(30, 362.1) * mm, "end": v(30, 312.1) * mm});
            skLineSegment(sketch, "E147.right", {"start": v(50, 362.1) * mm, "end": v(50, 312.1) * mm});
            skPoint(sketch, "E147.middle", {"position": v(40, 337.1) * mm});
            skPoint(sketch, "E147.middle.positionSnap0", {"position": v(40, 470) * mm});
            skPoint(sketch, "E147.centerSnap0", {"position": v(40, 470) * mm});
            skLineSegment(sketch, "E148", {"start": v(30, 362.1) * mm, "end": v(40, 350.1) * mm});
            skLineSegment(sketch, "E149", {"start": v(40, 350.1) * mm, "end": v(50, 362.1) * mm});
            skLineSegment(sketch, "E150", {"start": v(30, 312.1) * mm, "end": v(40, 324.1) * mm});
            skPoint(sketch, "E150.endSnap0", {"position": v(40, 312.1) * mm});
            skLineSegment(sketch, "E151", {"start": v(40, 324.1) * mm, "end": v(50, 312.1) * mm});
            skSolve(sketch);
        }
        {
            var Q0;
            Q0=makeQuery(id+"F15.imprint","IMPRINT",FACE,{"disambiguationData":[TD([[makeQuery(id+"F15.imprint","IMPRINT",EDGE,{"derivedFrom":sQuery(id+"F15.wireOp",EDGE,"E147.left")}),1.0]])]});
            extrude(context, id + "F16", {"entities" : qUnion([Q0]), "operationType" : NewBodyOperationType.REMOVE, "oppositeDirection" : true, "depth" : 10 * mm});
        }
        {
            var Q0;
            Q0=makeQuery(id+"F12.opExtrude","SWEPT_FACE",FACE,{"disambiguationData":[OSD([sQuery(id+"F11.wireOp",EDGE,"E141")])]});
            var sketch = newSketch(context, id + "F17", { "sketchPlane" : qUnion([Q0])});
            skLineSegment(sketch, "E152.bottom", {"start": v(30, 75) * mm, "end": v(50, 75) * mm});
            skLineSegment(sketch, "E152.top", {"start": v(30, 25) * mm, "end": v(50, 25) * mm});
            skLineSegment(sketch, "E152.left", {"start": v(30, 75) * mm, "end": v(30, 25) * mm});
            skLineSegment(sketch, "E152.right", {"start": v(50, 75) * mm, "end": v(50, 25) * mm});
            skPoint(sketch, "E152.middle", {"position": v(40, 50) * mm});
            skPoint(sketch, "E152.middle.positionSnap0", {"position": v(40, 0) * mm});
            skPoint(sketch, "E152.centerSnap0", {"position": v(40, 0) * mm});
            skLineSegment(sketch, "E153", {"start": v(30, 75) * mm, "end": v(40, 69) * mm});
            skPoint(sketch, "E153.endSnap0", {"position": v(40, 25) * mm});
            skLineSegment(sketch, "E154", {"start": v(40, 69) * mm, "end": v(50, 75) * mm});
            skLineSegment(sketch, "E155", {"start": v(30, 25) * mm, "end": v(40, 31) * mm});
            skLineSegment(sketch, "E156", {"start": v(40, 31) * mm, "end": v(50, 25) * mm});
            skSolve(sketch);
        }
        {
            var Q0;
            Q0=makeQuery(id+"F17.imprint","IMPRINT",FACE,{"disambiguationData":[TD([[makeQuery(id+"F17.imprint","IMPRINT",EDGE,{"derivedFrom":sQuery(id+"F17.wireOp",EDGE,"E152.left")}),1.0]])]});
            extrude(context, id + "F18", {"entities" : qUnion([Q0]), "operationType" : NewBodyOperationType.REMOVE, "oppositeDirection" : true, "depth" : 10 * mm});
        }
        {
            var Q0;
            Q0=makeQuery(id+"F12.opExtrude","SWEPT_FACE",FACE,{"disambiguationData":[OSD([sQuery(id+"F11.wireOp",EDGE,"E139.top")])]});
            var sketch = newSketch(context, id + "F19", { "sketchPlane" : qUnion([Q0])});
            skLineSegment(sketch, "E157", {"start": v(40, 350.1) * mm, "end": v(40, 375.1) * mm});
            skLineSegment(sketch, "E158", {"start": v(40, 375.1) * mm, "end": v(40.25, 375.1) * mm});
            skLineSegment(sketch, "E159", {"start": v(40.25, 375.1) * mm, "end": v(40.25, 350.4) * mm});
            skLineSegment(sketch, "E160", {"start": v(40, 375.1) * mm, "end": v(39.75, 375.1) * mm});
            skLineSegment(sketch, "E161", {"start": v(39.75, 375.1) * mm, "end": v(39.75, 350.4) * mm});
            skLineSegment(sketch, "E162", {"start": v(39.75, 350.4) * mm, "end": v(40, 350.1) * mm});
            skLineSegment(sketch, "E163", {"start": v(40.25, 350.4) * mm, "end": v(40, 350.1) * mm});
            skLineSegment(sketch, "E164", {"start": v(40, 324.1) * mm, "end": v(40, 299.1) * mm});
            skLineSegment(sketch, "E165", {"start": v(40, 299.1) * mm, "end": v(40.25, 299.1) * mm});
            skLineSegment(sketch, "E166", {"start": v(40.25, 299.1) * mm, "end": v(40.25, 323.8) * mm});
            skLineSegment(sketch, "E167", {"start": v(40.25, 323.8) * mm, "end": v(40, 324.1) * mm});
            skLineSegment(sketch, "E168", {"start": v(40, 299.1) * mm, "end": v(39.75, 299.1) * mm});
            skLineSegment(sketch, "E169", {"start": v(39.75, 299.1) * mm, "end": v(39.75, 323.8) * mm});
            skLineSegment(sketch, "E170", {"start": v(39.75, 323.8) * mm, "end": v(40, 324.1) * mm});
            skSolve(sketch);
        }
        {
            var Q0;
            Q0=qSketchRegion(id+"F19",true);
            extrude(context, id + "F20", {"entities" : qUnion([Q0]), "operationType" : NewBodyOperationType.REMOVE, "oppositeDirection" : true, "depth" : 0.5 * mm});
        }
        {
            var Q0;
            Q0=makeQuery(id+"F12.opExtrude","SWEPT_FACE",FACE,{"disambiguationData":[OSD([sQuery(id+"F11.wireOp",EDGE,"E141")])]});
            var sketch = newSketch(context, id + "F21", { "sketchPlane" : qUnion([Q0])});
            skLineSegment(sketch, "E171", {"start": v(40, 69) * mm, "end": v(40, 79) * mm});
            skLineSegment(sketch, "E172", {"start": v(40, 79) * mm, "end": v(40.25, 79) * mm});
            skLineSegment(sketch, "E173", {"start": v(40.25, 79) * mm, "end": v(40.25, 69.15) * mm});
            skLineSegment(sketch, "E174", {"start": v(40.25, 69.15) * mm, "end": v(40, 69) * mm});
            skLineSegment(sketch, "E175", {"start": v(40, 79) * mm, "end": v(39.75, 79) * mm});
            skLineSegment(sketch, "E176", {"start": v(39.75, 79) * mm, "end": v(39.75, 69.15) * mm});
            skLineSegment(sketch, "E177", {"start": v(39.75, 69.15) * mm, "end": v(40, 69) * mm});
            skLineSegment(sketch, "E178", {"start": v(40, 31) * mm, "end": v(40, 21) * mm});
            skLineSegment(sketch, "E179", {"start": v(40, 21) * mm, "end": v(40.25, 21) * mm});
            skLineSegment(sketch, "E180", {"start": v(40.25, 21) * mm, "end": v(40.25, 30.85) * mm});
            skLineSegment(sketch, "E181", {"start": v(40.25, 30.85) * mm, "end": v(40, 31) * mm});
            skLineSegment(sketch, "E182", {"start": v(40, 21) * mm, "end": v(39.75, 21) * mm});
            skLineSegment(sketch, "E183", {"start": v(39.75, 21) * mm, "end": v(39.75, 30.85) * mm});
            skLineSegment(sketch, "E184", {"start": v(39.75, 30.85) * mm, "end": v(40, 31) * mm});
            skSolve(sketch);
        }
        {
            var Q0;
            Q0=qSketchRegion(id+"F21",true);
            extrude(context, id + "F22", {"entities" : qUnion([Q0]), "operationType" : NewBodyOperationType.REMOVE, "oppositeDirection" : true, "depth" : 0.25 * mm});
        }
        {
            var Q0;
            Q0=makeQuery(id+"F1.opExtrude","SWEPT_EDGE",EDGE,{"disambiguationData":[OSD([sQuery(id+"F0.wireOp",EDGE,"E33"),sQuery(id+"F0.wireOp",EDGE,"E34")])]});
            var Q1;
            Q1=makeQuery(id+"F1.opExtrude","SWEPT_EDGE",EDGE,{"disambiguationData":[OSD([sQuery(id+"F0.wireOp",EDGE,"E29"),sQuery(id+"F0.wireOp",EDGE,"E30")])]});
            fillet(context, id + "F23", {"entities" : qUnion([Q0, Q1]), "radius" : 50 * mm, "tangentPropagation" : true, "allowEdgeOverflow" : false});
        }
        {
            var Q0;
            Q0=makeQuery(id+"F1.opExtrude","SWEPT_EDGE",EDGE,{"disambiguationData":[OSD([sQuery(id+"F0.wireOp",EDGE,"E27"),sQuery(id+"F0.wireOp",EDGE,"E28")])]});
            var Q1;
            Q1=makeQuery(id+"F1.opExtrude","SWEPT_EDGE",EDGE,{"disambiguationData":[OSD([sQuery(id+"F0.wireOp",EDGE,"E32"),sQuery(id+"F0.wireOp",EDGE,"E33")])]});
            var Q2;
            Q2=makeQuery(id+"F1.opExtrude","SWEPT_EDGE",EDGE,{"disambiguationData":[OSD([sQuery(id+"F0.wireOp",EDGE,"E23"),sQuery(id+"F0.wireOp",EDGE,"E24")])]});
            fillet(context, id + "F24", {"entities" : qUnion([Q0, Q1, Q2]), "radius" : 20 * mm, "tangentPropagation" : true, "allowEdgeOverflow" : false});
        }
        {
            var Q0;
            Q0=makeQuery(id+"F12.opExtrude","CAP_EDGE",EDGE,{"disambiguationData":[OSD([sQuery(id+"F11.wireOp",EDGE,"E142")])],"isStart":true});
            var Q1;
            Q1=makeQuery(id+"F12.opExtrude","CAP_EDGE",EDGE,{"disambiguationData":[OSD([sQuery(id+"F11.wireOp",EDGE,"E142")])],"isStart":false});
            var Q2;
            Q2=makeQuery(id+"F12.opExtrude","CAP_EDGE",EDGE,{"disambiguationData":[OSD([sQuery(id+"F11.wireOp",EDGE,"E139.left")])],"isStart":false});
            var Q3;
            Q3=makeQuery(id+"F12.opExtrude","CAP_EDGE",EDGE,{"disambiguationData":[OSD([sQuery(id+"F11.wireOp",EDGE,"E139.left")])],"isStart":true});
            fillet(context, id + "F25", {"entities" : qUnion([Q0, Q1, Q2, Q3]), "radius" : 20 * mm, "tangentPropagation" : true, "allowEdgeOverflow" : false});
        }
        {
            var Q0;
            Q0=makeQuery(id+"F12.opExtrude","SWEPT_EDGE",EDGE,{"disambiguationData":[OSD([sQuery(id+"F11.wireOp",EDGE,"E140"),sQuery(id+"F11.wireOp",EDGE,"E141")])]});
            var Q1;
            Q1=makeQuery(id+"F12.opExtrude","SWEPT_EDGE",EDGE,{"disambiguationData":[OSD([sQuery(id+"F11.wireOp",EDGE,"E139.bottom"),sQuery(id+"F11.wireOp",EDGE,"E144")])]});
            fillet(context, id + "F26", {"entities" : qUnion([Q0, Q1]), "radius" : 10 * mm, "tangentPropagation" : true, "allowEdgeOverflow" : false});
        }
        {
            var Q0;
            Q0=makeQuery(id+"F12.opExtrude","SWEPT_EDGE",EDGE,{"disambiguationData":[OSD([sQuery(id+"F11.wireOp",EDGE,"E139.top"),sQuery(id+"F11.wireOp",EDGE,"E140")])]});
            var Q1;
            Q1=makeQuery(id+"F12.opExtrude","SWEPT_EDGE",EDGE,{"disambiguationData":[OSD([sQuery(id+"F11.wireOp",EDGE,"E143"),sQuery(id+"F11.wireOp",EDGE,"E144")])]});
            fillet(context, id + "F27", {"entities" : qUnion([Q0, Q1]), "radius" : 5 * mm, "tangentPropagation" : true, "allowEdgeOverflow" : false});
        }
        {
            var Q0;
            Q0=qCreatedBy(makeId("Right.planeOp"),FACE);
            var sketch = newSketch(context, id + "F28", { "sketchPlane" : qUnion([Q0])});
            skArc(sketch, "E185", {"start": v(-47.48, 41.9) * mm, "mid": v(-68.98, 63.4) * mm, "end": v(-90.48, 41.9) * mm});
            skLineSegment(sketch, "E186", {"start": v(-47.48, 41.9) * mm, "end": v(-47.48, 20.4) * mm});
            skLineSegment(sketch, "E187", {"start": v(-90.48, 41.9) * mm, "end": v(-90.48, 20.4) * mm});
            skSolve(sketch);
        }
        {
            var Q0;
            Q0=sQuery(id+"F28.wireOp",VERTEX,"E187.end");
            var Q1;
            Q1=qCreatedBy(makeId("Top.planeOp"),FACE);
            cPlane(context, id + "F29", {"entities" : qUnion([Q0, Q1]), "cplaneType" : CPlaneType.PLANE_POINT, "offset" : 25 * mm, "width" : 150 * mm, "height" : 150 * mm});
        }
        {
            var Q0;
            Q0=qCreatedBy(id+"F29.planeOp",FACE);
            var sketch = newSketch(context, id + "F30", { "sketchPlane" : qUnion([Q0])});
            skCircle(sketch, "E188", {"center": v(0, -90.48) * mm, "radius": 5 * mm});
            skSolve(sketch);
        }
        {
            var Q0;
            Q0=makeQuery(id+"F30.imprint","IMPRINT",FACE,{"disambiguationData":[TD([[makeQuery(id+"F30.imprint","IMPRINT",EDGE,{"derivedFrom":sQuery(id+"F30.wireOp",EDGE,"E188")}),1.0]])]});
            var Q1;
            Q1=sQuery(id+"F28.wireOp",EDGE,"E187");
            var Q2;
            Q2=sQuery(id+"F28.wireOp",EDGE,"E185");
            var Q3;
            Q3=sQuery(id+"F28.wireOp",EDGE,"E186");
            sweep(context, id + "F31", {"profiles" : qUnion([Q0]), "path" : qUnion([Q1, Q2, Q3])});
        }
        {
            var Q0;
            Q0=qCreatedBy(makeId("Right.planeOp"),FACE);
            var sketch = newSketch(context, id + "F32", { "sketchPlane" : qUnion([Q0])});
            skLineSegment(sketch, "E189", {"start": v(-114.2, 20.99) * mm, "end": v(-139.2, 20.99) * mm});
            skArc(sketch, "E190", {"start": v(-139.2, 40.56) * mm, "mid": v(-158.2, 59.56) * mm, "end": v(-177.2, 40.56) * mm});
            skArc(sketch, "E191.0", {"start": v(-134.2, 40.56) * mm, "mid": v(-158.2, 64.56) * mm, "end": v(-182.2, 40.56) * mm});
            skLineSegment(sketch, "E192.left", {"start": v(-139.2, 40.56) * mm, "end": v(-139.2, 20.99) * mm});
            skLineSegment(sketch, "E192.right", {"start": v(-134.2, 40.56) * mm, "end": v(-134.2, 26.56) * mm});
            skLineSegment(sketch, "E193.left", {"start": v(-177.2, 40.56) * mm, "end": v(-177.2, 20.99) * mm});
            skLineSegment(sketch, "E193.right", {"start": v(-182.2, 40.56) * mm, "end": v(-182.2, 26.56) * mm});
            skLineSegment(sketch, "E194", {"start": v(-134.2, 26.56) * mm, "end": v(-114.2, 26.56) * mm});
            skLineSegment(sketch, "E195", {"start": v(-114.2, 26.56) * mm, "end": v(-114.2, 20.99) * mm});
            skLineSegment(sketch, "E196", {"start": v(-182.2, 26.56) * mm, "end": v(-202.2, 26.56) * mm});
            skLineSegment(sketch, "E197", {"start": v(-202.2, 26.56) * mm, "end": v(-202.2, 20.99) * mm});
            skPoint(sketch, "E198.orphan", {"position": v(-139.2, 16.56) * mm});
            skLineSegment(sketch, "E199.trimOffspring", {"start": v(-177.2, 20.99) * mm, "end": v(-220.09, 20.99) * mm});
            skPoint(sketch, "E200.trimOffspring.end.orphan", {"position": v(-182.2, 16.56) * mm});
            skSolve(sketch);
        }
        {
            var Q0;
            Q0=qSketchRegion(id+"F32",true);
            extrude(context, id + "F33", {"entities" : qUnion([Q0]), "depth" : 25 * mm});
        }
        {
            var Q0;
            Q0=qCreatedBy(makeId("Front.planeOp"),FACE);
            var sketch = newSketch(context, id + "F34", { "sketchPlane" : qUnion([Q0])});
            skLineSegment(sketch, "E201.bottom", {"start": v(136.6, 70.24) * mm, "end": v(187.4, 70.24) * mm});
            skLineSegment(sketch, "E201.top", {"start": v(136.6, 63.39) * mm, "end": v(187.4, 63.39) * mm});
            skLineSegment(sketch, "E201.left", {"start": v(136.6, 70.24) * mm, "end": v(136.6, 63.39) * mm});
            skLineSegment(sketch, "E201.right", {"start": v(187.4, 70.24) * mm, "end": v(187.4, 63.39) * mm});
            skSolve(sketch);
        }
        {
            var Q0;
            Q0 = qSketchRegion(id + "F34", true);
            extrude(context, id + "F35", {"entities" : qUnion([Q0]), "depth" : 64 * mm});
        }
        {
            var Q0;
            Q0=qCreatedBy(makeId("Front.planeOp"),FACE);
            var sketch = newSketch(context, id + "F36", { "sketchPlane" : qUnion([Q0])});
            skLineSegment(sketch, "E202.bottom", {"start": v(263.2, 43.75) * mm, "end": v(301.7, 43.75) * mm});
            skLineSegment(sketch, "E202.top", {"start": v(263.2, 25.75) * mm, "end": v(301.7, 25.75) * mm});
            skLineSegment(sketch, "E202.left", {"start": v(263.2, 43.75) * mm, "end": v(263.2, 25.75) * mm});
            skLineSegment(sketch, "E202.right", {"start": v(301.7, 43.75) * mm, "end": v(301.7, 25.75) * mm});
            skSolve(sketch);
        }
        {
            var Q0;
            Q0 = qSketchRegion(id + "F36", true);
            extrude(context, id + "F37", {"entities" : qUnion([Q0]), "depth" : 39.8 * mm});
        }
        {
            var Q0;
            Q0=sQuery(id+"F6.wireOp",VERTEX,"E51.center");
            var Q1;
            Q1=sQuery(id+"F6.wireOp",VERTEX,"E58.MirrorC.center");
            var Q2;
            Q2=sQuery(id+"F6.wireOp",VERTEX,"E60.center");
            var Q3;
            Q3=sQuery(id+"F6.wireOp",VERTEX,"E53.start");
            var Q4;
            Q4=sQuery(id+"F6.wireOp",VERTEX,"E53.end");
            var Q5;
            Q5=sQuery(id+"F6.wireOp",VERTEX,"E56.center");
            var Q6;
            Q6=sQuery(id+"F6.wireOp",VERTEX,"E43.center");
            var Q7;
            Q7=sQuery(id+"F6.wireOp",VERTEX,"E57.start");
            var Q8;
            Q8=makeQuery(id+"F1.opExtrude","SWEPT_BODY",BODY,{"disambiguationData":[OSD([sQuery(id+"F0.wireOp",EDGE,"E3"),sQuery(id+"F0.wireOp",EDGE,"E4"),sQuery(id+"F0.wireOp",EDGE,"E14"),sQuery(id+"F0.wireOp",EDGE,"E20"),sQuery(id+"F0.wireOp",EDGE,"E23"),sQuery(id+"F0.wireOp",EDGE,"E24"),sQuery(id+"F0.wireOp",EDGE,"E27"),sQuery(id+"F0.wireOp",EDGE,"E28"),sQuery(id+"F0.wireOp",EDGE,"E29"),sQuery(id+"F0.wireOp",EDGE,"E30"),sQuery(id+"F0.wireOp",EDGE,"E32"),sQuery(id+"F0.wireOp",EDGE,"E33"),sQuery(id+"F0.wireOp",EDGE,"E34")])]});
            hole(context, id + "F38", {"style" : HoleStyle.SIMPLE, "endStyle" : HoleEndStyle.THROUGH, "holeDiameter" : 8 * mm, "locations" : qUnion([Q0, Q1, Q2, Q3, Q4, Q5, Q6, Q7]), "scope" : qUnion([Q8]), "isTappedThrough" : true});
        }
    });
